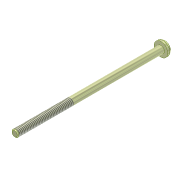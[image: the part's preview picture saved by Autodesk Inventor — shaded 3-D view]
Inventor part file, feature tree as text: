
AUTODESK INVENTOR PART (.ipt)
format: ipt  version: 2014 (Build 180170000, 170)  size: 104,448 bytes
history: native  units: mm
features: imported_body x1, thread x1
ambient origin geometry x8: Origin, YZ Plane, XZ Plane, XY Plane, X Axis, Y Axis, Z Axis, Center Point
bodies: Solid1 (feature_tree)
feature tree (2):
  imported_body  "Base1"
  thread  "Thread1"  [1 undecoded]
note: 1 required parameter value undecoded (feature->parameter linkage not recoverable at this tier; creation-order binding heuristic only, values carry confidence <= 0.55)
